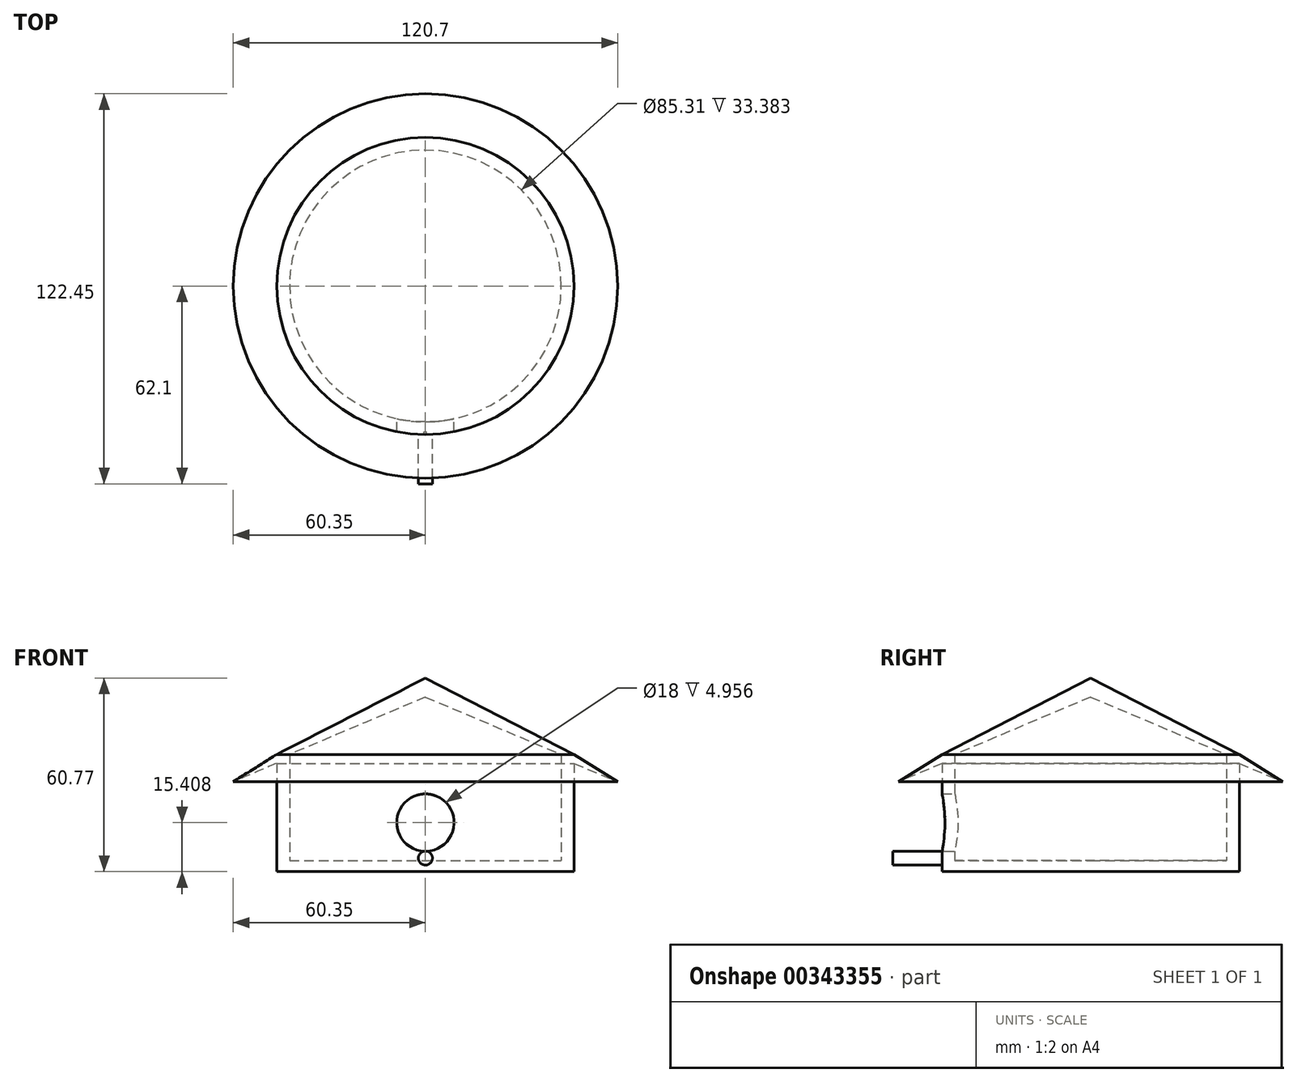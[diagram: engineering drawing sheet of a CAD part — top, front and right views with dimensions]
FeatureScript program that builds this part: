
annotation { "Feature Type Name" : "Feature", "Feature Type Description" : "" }
export const myFeature = defineFeature(function(context is Context, id is Id, definition is map)
    precondition{}
    {
        {
            var Q0;
            Q0=qCreatedBy(makeId("Front.planeOp"),FACE);
            var sketch = newSketch(context, id + "F0", { "sketchPlane" : qUnion([Q0])});
            skLineSegment(sketch, "E0.bottom", {"start": v(0, 0) * mm, "end": v(42.66, 0) * mm});
            skLineSegment(sketch, "E0.top", {"start": v(0, 3.42) * mm, "end": v(42.66, 3.42) * mm});
            skLineSegment(sketch, "E0.left", {"start": v(0, 0) * mm, "end": v(0, 3.42) * mm});
            skLineSegment(sketch, "E1.bottom", {"start": v(42.66, 0) * mm, "end": v(46.65, 0) * mm});
            skLineSegment(sketch, "E1.left", {"start": v(42.66, 3.42) * mm, "end": v(42.66, 36.8) * mm});
            skLineSegment(sketch, "E1.right", {"start": v(46.65, 0) * mm, "end": v(46.65, 34.02) * mm});
            skLineSegment(sketch, "E2", {"start": v(0, 54.78) * mm, "end": v(42.66, 36.8) * mm});
            skLineSegment(sketch, "E3", {"start": v(0, 54.78) * mm, "end": v(0, 60.77) * mm});
            skLineSegment(sketch, "E4", {"start": v(0, 60.77) * mm, "end": v(46.65, 36.8) * mm});
            skLineSegment(sketch, "E5", {"start": v(46.65, 36.8) * mm, "end": v(60.35, 28.25) * mm});
            skLineSegment(sketch, "E6", {"start": v(60.35, 28.25) * mm, "end": v(46.65, 34.02) * mm});
            skSolve(sketch);
        }
        {
            var Q0;
            Q0 = qSketchRegion(id + "F0", true);
            var Q1;
            Q1=sQuery(id+"F0.wireOp",EDGE,"E0.left");
            revolve(context, id + "F1", {"entities" : qUnion([Q0]), "axis" : qUnion([Q1]), "revolveType" : RevolveType.FULL});
        }
        {
            var Q0;
            Q0=qCreatedBy(makeId("Front.planeOp"),FACE);
            var sketch = newSketch(context, id + "F2", { "sketchPlane" : qUnion([Q0])});
            skCircle(sketch, "E7", {"center": v(0, 15.4) * mm, "radius": 9 * mm});
            skSolve(sketch);
        }
        {
            var Q0;
            Q0 = qSketchRegion(id + "F2", true);
            extrude(context, id + "F3", {"entities" : qUnion([Q0]), "operationType" : NewBodyOperationType.REMOVE, "depth" : 67.8 * mm});
        }
        {
            var Q0;
            Q0=qCreatedBy(makeId("Front.planeOp"),FACE);
            cPlane(context, id + "F4", {"entities" : qUnion([Q0]), "cplaneType" : CPlaneType.OFFSET, "offset" : 45.8 * mm, "width" : 150 * mm, "height" : 150 * mm});
        }
        {
            var Q0;
            Q0=qCreatedBy(id+"F4.planeOp",FACE);
            var sketch = newSketch(context, id + "F5", { "sketchPlane" : qUnion([Q0])});
            skCircle(sketch, "E8", {"center": v(0, 4.25) * mm, "radius": 2.2 * mm});
            skSolve(sketch);
        }
        {
            var Q0;
            Q0 = qSketchRegion(id + "F5", true);
            extrude(context, id + "F6", {"entities" : qUnion([Q0]), "operationType" : NewBodyOperationType.ADD, "depth" : 16.3 * mm});
        }
    });
